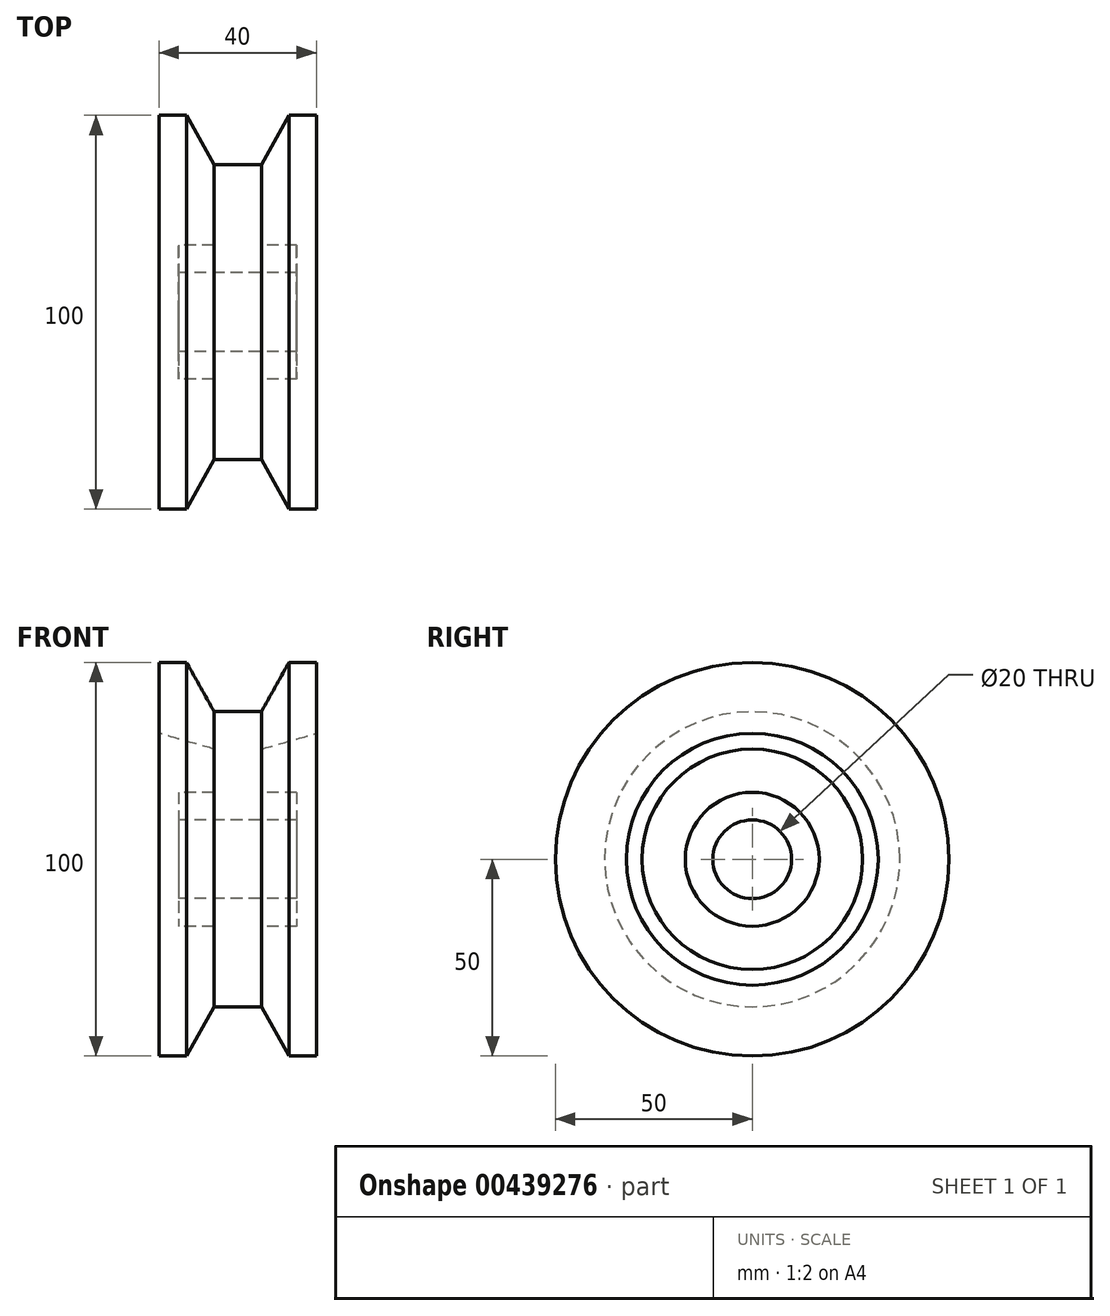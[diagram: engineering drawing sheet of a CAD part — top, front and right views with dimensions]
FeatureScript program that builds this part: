
annotation { "Feature Type Name" : "Feature", "Feature Type Description" : "" }
export const myFeature = defineFeature(function(context is Context, id is Id, definition is map)
    precondition{}
    {
        {
            var Q0;
            Q0=qCreatedBy(makeId("Front.planeOp"),FACE);
            var sketch = newSketch(context, id + "F0", { "sketchPlane" : qUnion([Q0])});
            skLineSegment(sketch, "E0", {"start": v(0, 0) * mm, "end": v(5.1, 0) * mm});
            skLineSegment(sketch, "E1", {"start": v(-15, -17) * mm, "end": v(-15, -10) * mm});
            skLineSegment(sketch, "E2", {"start": v(-15, -10) * mm, "end": v(15, -10) * mm});
            skLineSegment(sketch, "E3", {"start": v(15, -10) * mm, "end": v(15, -17) * mm});
            skLineSegment(sketch, "E4", {"start": v(15, -17) * mm, "end": v(6, -17) * mm});
            skLineSegment(sketch, "E5", {"start": v(6, -17) * mm, "end": v(6, -28) * mm});
            skLineSegment(sketch, "E6", {"start": v(-15, -17) * mm, "end": v(-6, -17) * mm});
            skLineSegment(sketch, "E7", {"start": v(-6, -17) * mm, "end": v(-6, -28) * mm});
            skLineSegment(sketch, "E8", {"start": v(-6, -28) * mm, "end": v(-20, -32) * mm});
            skLineSegment(sketch, "E9", {"start": v(6, -28) * mm, "end": v(20, -32) * mm});
            skLineSegment(sketch, "E10", {"start": v(-20, -32) * mm, "end": v(-20, -50) * mm});
            skLineSegment(sketch, "E11", {"start": v(-20, -50) * mm, "end": v(-13, -50) * mm});
            skLineSegment(sketch, "E12", {"start": v(-13, -50) * mm, "end": v(-6, -37.5) * mm});
            skLineSegment(sketch, "E13", {"start": v(-6, -37.5) * mm, "end": v(6, -37.5) * mm});
            skLineSegment(sketch, "E14", {"start": v(6, -37.5) * mm, "end": v(13, -50) * mm});
            skLineSegment(sketch, "E15", {"start": v(13, -50) * mm, "end": v(20, -50) * mm});
            skLineSegment(sketch, "E16", {"start": v(20, -50) * mm, "end": v(20, -32) * mm});
            skSolve(sketch);
        }
        {
            var Q0;
            Q0=makeQuery(id+"F0.imprint","IMPRINT",FACE,{"disambiguationData":[TD([[makeQuery(id+"F0.imprint","IMPRINT",EDGE,{"derivedFrom":sQuery(id+"F0.wireOp",EDGE,"E1")}),-1.0]])]});
            var Q1;
            Q1=sQuery(id+"F0.wireOp",EDGE,"E0");
            revolve(context, id + "F1", {"entities" : qUnion([Q0]), "axis" : qUnion([Q1]), "revolveType" : RevolveType.FULL});
        }
    });
